# Revit family: Shower-Valve-KOHLER-MASTERSHOWER-728W
name_source: partatom
category: Plumbing Fixtures
revit_build: Autodesk Revit 2017 (Build: 20160225_1515(x64)
units: mm (PartAtom-declared; Revit-internal decimal feet)

## family parameters
Cut with Voids When Loaded = No
Host = Face
OmniClass Number = 23.27.31.00
OmniClass Title = Valves
Part Type = Normal
Room Calculation Point = No
Round Connector Dimension = Use Diameter
Shared = No

## types (1)
- NA-Stainless Steel
    ADA Compliant = No
    Assembly Code = D2020
    CW Connection = Yes
    Cold Water Inlet = Cold Water Inlet
    Cold Water Outlet = Cold Water Outlet
    Date Modified = 03/05/2021
    Default Elevation = 36"
    Description = 2 OR 3 WAY TRANSFER VALVE
    Finish = Kohler-Metal-NA-Stainless_Steel_Wire_Drawing
    Flow Rate = 0 GPM
    HW Connection = Yes
    Height = 4 9/16"
    Hot Water Inlet = Hot Water Inlet
    Hot Water Outlet = Hot Water Outlet
    Length = 3 1/4"
    Manufacturer = KOHLER Co.
    Master Format 2014 = 23 09 13.33
    Master Format 2014 Name = Control Valves
    Material = Zinc
    Model = 728W-K-NA
    Pressure = 0.00 psi
    Product Name = MASTERSHOWER
    Tempered Water Inlet = Tempered Water Inlet
    Tempered Water Outlet = Tempered Water Outlet
    Type = 1
    URL = https://www.kohler.co.uk
    Vent Connection = No
    Waste Connection = No
    Waste Water Outlet = Waste Water Outlet
    WaterSense Certified = No
    Width = 3"

## geometry (parser evidence)
native form markers: Sweep x4
no freeform markers — native parametric forms only
